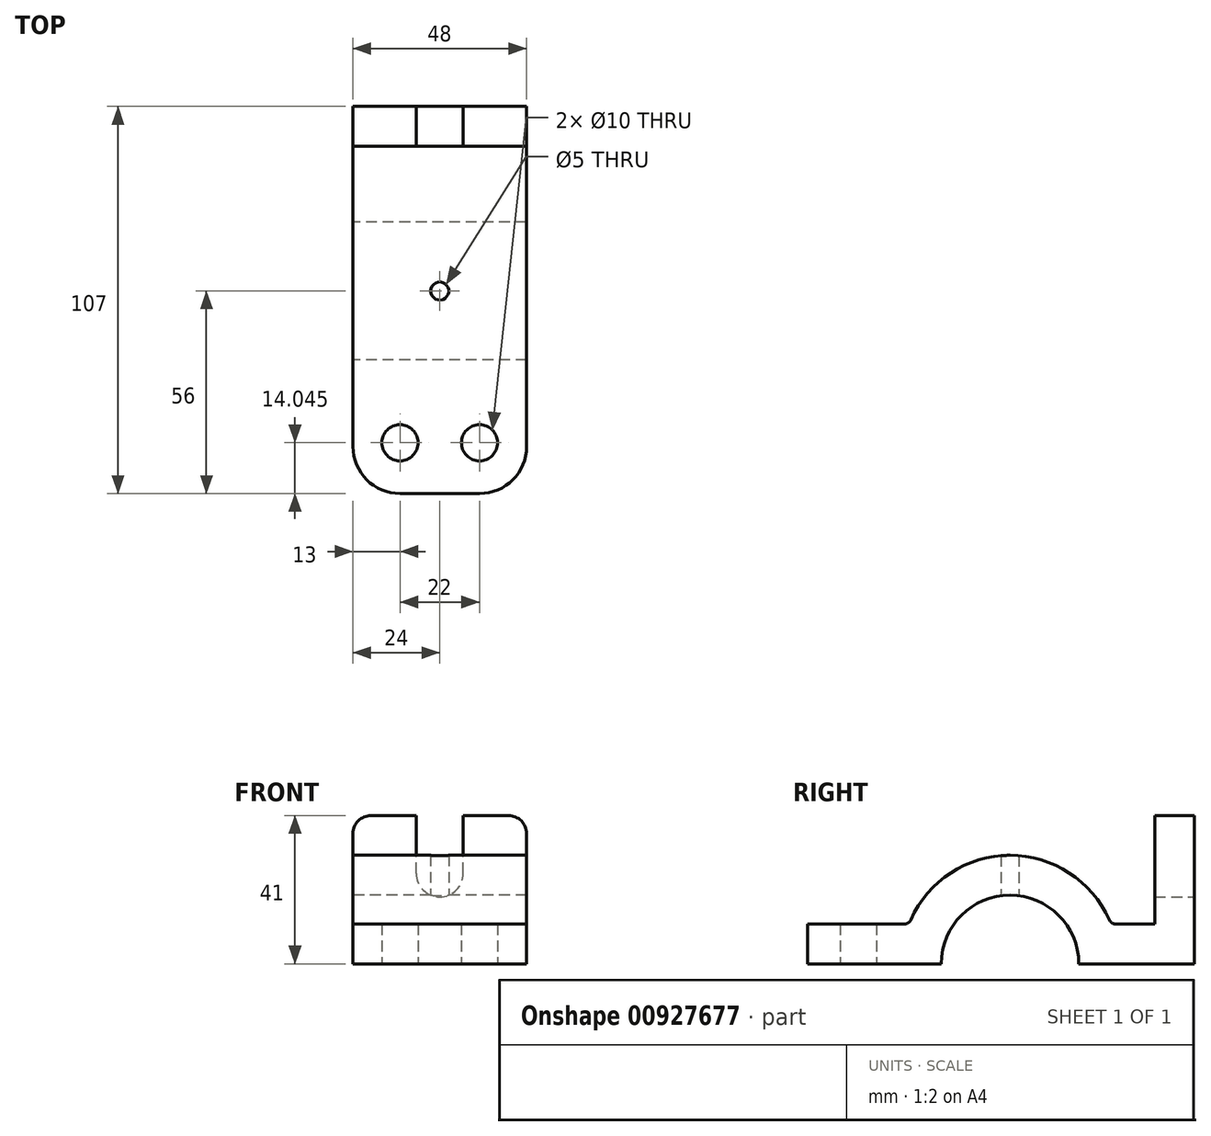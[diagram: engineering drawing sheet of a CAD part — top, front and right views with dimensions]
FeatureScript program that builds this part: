
annotation { "Feature Type Name" : "Feature", "Feature Type Description" : "" }
export const myFeature = defineFeature(function(context is Context, id is Id, definition is map)
    precondition{}
    {
        {
            var Q0;
            Q0=qCreatedBy(makeId("Right.planeOp"),FACE);
            var sketch = newSketch(context, id + "F0", { "sketchPlane" : qUnion([Q0])});
            skCircle(sketch, "E0", {"center": v(0, 0) * mm, "radius": 19 * mm});
            skCircle(sketch, "E1", {"center": v(0, 0) * mm, "radius": 30 * mm});
            skLineSegment(sketch, "E2.bottom", {"start": v(-56, 0) * mm, "end": v(51, 0) * mm});
            skLineSegment(sketch, "E2.top", {"start": v(-56, 11) * mm, "end": v(51, 11) * mm});
            skLineSegment(sketch, "E2.left", {"start": v(-56, 0) * mm, "end": v(-56, 11) * mm});
            skLineSegment(sketch, "E2.right", {"start": v(51, 0) * mm, "end": v(51, 11) * mm});
            skLineSegment(sketch, "E3.bottom", {"start": v(51, 11) * mm, "end": v(40, 11) * mm});
            skLineSegment(sketch, "E3.top", {"start": v(51, 41) * mm, "end": v(40, 41) * mm});
            skLineSegment(sketch, "E3.left", {"start": v(51, 11) * mm, "end": v(51, 41) * mm});
            skLineSegment(sketch, "E3.right", {"start": v(40, 11) * mm, "end": v(40, 41) * mm});
            skSolve(sketch);
        }
        {
            var Q0;
            {var subQ5=sQuery(id+"F0.wireOp",EDGE,"E2.left");Q0=makeQuery(id+"F0.imprint","IMPRINT",FACE,{"disambiguationData":[TD([[makeQuery(id+"F0.imprint","IMPRINT",EDGE,{"derivedFrom":subQ5}),-1.0]])]});}
            var Q1;
            {var subQ0=sQuery(id+"F0.wireOp",EDGE,"E2.bottom");var subQ1=sQuery(id+"F0.wireOp",EDGE,"E0");var subQ2=makeQuery(id+"F0.imprint","INTERSECT",VERTEX,{"disambiguationData":[OD(0.0)],"derivedFrom":[subQ1,subQ0]});Q1=makeQuery(id+"F0.imprint","IMPRINT",FACE,{"disambiguationData":[TD([[makeQuery(id+"F0.imprint","IMPRINT",EDGE,{"disambiguationData":[TD([[subQ2,1.0]])],"derivedFrom":subQ1}),-1.0]])]});}
            var Q2;
            {var subQ0=sQuery(id+"F0.wireOp",EDGE,"E2.top");var subQ1=sQuery(id+"F0.wireOp",EDGE,"E0");var subQ2=makeQuery(id+"F0.imprint","INTERSECT",VERTEX,{"disambiguationData":[OD(0.0)],"derivedFrom":[subQ1,subQ0]});Q2=makeQuery(id+"F0.imprint","IMPRINT",FACE,{"disambiguationData":[TD([[makeQuery(id+"F0.imprint","IMPRINT",EDGE,{"disambiguationData":[TD([[subQ2,1.0]])],"derivedFrom":subQ1}),-1.0]])]});}
            var Q3;
            {var subQ0=sQuery(id+"F0.wireOp",EDGE,"E2.top");var subQ1=sQuery(id+"F0.wireOp",EDGE,"E0");var subQ2=makeQuery(id+"F0.imprint","INTERSECT",VERTEX,{"disambiguationData":[OD(1.0)],"derivedFrom":[subQ1,subQ0]});Q3=makeQuery(id+"F0.imprint","IMPRINT",FACE,{"disambiguationData":[TD([[makeQuery(id+"F0.imprint","IMPRINT",EDGE,{"disambiguationData":[TD([[subQ2,1.0]])],"derivedFrom":subQ1}),-1.0]])]});}
            var Q4;
            {var subQ0=sQuery(id+"F0.wireOp",EDGE,"E2.right");Q4=makeQuery(id+"F0.imprint","IMPRINT",FACE,{"disambiguationData":[TD([[makeQuery(id+"F0.imprint","IMPRINT",EDGE,{"derivedFrom":subQ0}),1.0]])]});}
            var Q5;
            Q5=makeQuery(id+"F0.imprint","IMPRINT",FACE,{"disambiguationData":[TD([[makeQuery(id+"F0.imprint","IMPRINT",EDGE,{"derivedFrom":sQuery(id+"F0.wireOp",EDGE,"E3.top")}),1.0]])]});
            extrude(context, id + "F1", {"entities" : qUnion([Q0, Q1, Q2, Q3, Q4, Q5]), "endBound" : BoundingType.SYMMETRIC, "depth" : 48 * mm});
        }
        {
            var Q0;
            Q0=makeQuery(id+"F1.opExtrude","SWEPT_FACE",FACE,{"disambiguationData":[OSD([sQuery(id+"F0.wireOp",EDGE,"E2.right"),sQuery(id+"F0.wireOp",EDGE,"E3.left")])]});
            var sketch = newSketch(context, id + "F2", { "sketchPlane" : qUnion([Q0])});
            skLineSegment(sketch, "E4", {"start": v(0, 0) * mm, "end": v(0, 41) * mm, "construction": true});
            skCircle(sketch, "E5", {"center": v(0, 25) * mm, "radius": 6.5 * mm});
            skLineSegment(sketch, "E6", {"start": v(-6.5, 25) * mm, "end": v(-6.5, 41) * mm});
            skLineSegment(sketch, "E7", {"start": v(6.5, 25) * mm, "end": v(6.5, 41) * mm});
            skSolve(sketch);
        }
        {
            var Q0;
            {var subQ0=sQuery(id+"F2.wireOp",EDGE,"E5");var subQ2=makeQuery(id+"F2.imprint","INTERSECT",VERTEX,{"derivedFrom":[subQ0,sQuery(id+"F2.wireOp",EDGE,"E6")]});Q0=makeQuery(id+"F2.imprint","IMPRINT",FACE,{"disambiguationData":[TD([[makeQuery(id+"F2.imprint","IMPRINT",EDGE,{"disambiguationData":[TD([[subQ2,1.0]])],"derivedFrom":subQ0}),1.0]])]});}
            var Q1;
            {var subQ2=sQuery(id+"F2.wireOp",EDGE,"E6");Q1=makeQuery(id+"F2.imprint","IMPRINT",FACE,{"disambiguationData":[TD([[makeQuery(id+"F2.imprint","IMPRINT",EDGE,{"derivedFrom":subQ2}),-1.0]])]});}
            var Q2;
            Q2=makeQuery(id+"F1.opExtrude","SWEPT_FACE",FACE,{"disambiguationData":[OSD([sQuery(id+"F0.wireOp",EDGE,"E3.right")])]});
            extrude(context, id + "F3", {"entities" : qUnion([Q0, Q1]), "operationType" : NewBodyOperationType.REMOVE, "endBound" : BoundingType.UP_TO_SURFACE, "oppositeDirection" : true, "endBoundEntityFace" : qUnion([Q2]), "depth" : 25 * mm});
        }
        {
            var Q0;
            {var subQ0=sQuery(id+"F0.wireOp",EDGE,"E2.bottom");Q0=makeQuery(id+"F1.opExtrude","SWEPT_FACE",FACE,{"disambiguationData":[OSD([subQ0]),TDD([makeQuery(id+"F0.imprint","IMPRINT",EDGE,{"disambiguationData":[TD([[makeQuery(id+"F0.imprint","INTERSECT",VERTEX,{"derivedFrom":[subQ0,sQuery(id+"F0.wireOp",EDGE,"E2.left")]}),-1.0]])],"derivedFrom":subQ0}),makeQuery(id+"F0.imprint","IMPRINT",EDGE,{"disambiguationData":[TD([[makeQuery(id+"F0.imprint","INTERSECT",VERTEX,{"disambiguationData":[OD(0.0)],"derivedFrom":[sQuery(id+"F0.wireOp",EDGE,"E0"),subQ0]}),1.0]])],"derivedFrom":subQ0})])]});}
            var sketch = newSketch(context, id + "F4", { "sketchPlane" : qUnion([Q0])});
            skCircle(sketch, "E8", {"center": v(0, 0) * mm, "radius": 2.5 * mm});
            skLineSegment(sketch, "E9", {"start": v(24, 41.96) * mm, "end": v(-24, 41.96) * mm, "construction": true});
            skLineSegment(sketch, "E10", {"start": v(0, 27.91) * mm, "end": v(0, 56) * mm, "construction": true});
            skCircle(sketch, "E11", {"center": v(-11, 41.96) * mm, "radius": 5 * mm});
            skCircle(sketch, "E12", {"center": v(11, 41.96) * mm, "radius": 5 * mm});
            skSolve(sketch);
        }
        {
            var Q0;
            Q0=qSketchRegion(id+"F4",true);
            extrude(context, id + "F5", {"entities" : qUnion([Q0]), "operationType" : NewBodyOperationType.REMOVE, "endBound" : BoundingType.THROUGH_ALL, "oppositeDirection" : true, "depth" : 25 * mm, "offsetDistance" : 25 * mm});
        }
        {
            var Q0;
            Q0=makeQuery(id+"F1.opExtrude","CAP_EDGE",EDGE,{"disambiguationData":[OSD([sQuery(id+"F0.wireOp",EDGE,"E2.left")])],"isStart":false});
            var Q1;
            Q1=makeQuery(id+"F1.opExtrude","CAP_EDGE",EDGE,{"disambiguationData":[OSD([sQuery(id+"F0.wireOp",EDGE,"E2.left")])],"isStart":true});
            fillet(context, id + "F6", {"entities" : qUnion([Q0, Q1]), "radius" : 13 * mm, "tangentPropagation" : true, "allowEdgeOverflow" : false});
        }
        {
            var Q0;
            Q0=makeQuery(id+"F1.opExtrude","CAP_EDGE",EDGE,{"disambiguationData":[OSD([sQuery(id+"F0.wireOp",EDGE,"E3.top")])],"isStart":false});
            var Q1;
            Q1=makeQuery(id+"F1.opExtrude","CAP_EDGE",EDGE,{"disambiguationData":[OSD([sQuery(id+"F0.wireOp",EDGE,"E3.top")])],"isStart":true});
            fillet(context, id + "F7", {"entities" : qUnion([Q0, Q1]), "radius" : 5 * mm, "tangentPropagation" : true, "allowEdgeOverflow" : false});
        }
        {
            var Q0;
            {var subQ0=sQuery(id+"F0.wireOp",EDGE,"E2.top");var subQ1=sQuery(id+"F0.wireOp",EDGE,"E1");Q0=makeQuery(id+"F1.opExtrude","SWEPT_EDGE",EDGE,{"disambiguationData":[OSD([subQ1,subQ0]),TDD([makeQuery(id+"F0.imprint","INTERSECT",VERTEX,{"disambiguationData":[OD(1.0)],"derivedFrom":[subQ1,subQ0]})])]});}
            var Q1;
            {var subQ0=sQuery(id+"F0.wireOp",EDGE,"E2.top");var subQ1=sQuery(id+"F0.wireOp",EDGE,"E1");Q1=makeQuery(id+"F1.opExtrude","SWEPT_EDGE",EDGE,{"disambiguationData":[OSD([subQ1,subQ0]),TDD([makeQuery(id+"F0.imprint","INTERSECT",VERTEX,{"disambiguationData":[OD(0.0)],"derivedFrom":[subQ1,subQ0]})])]});}
            fillet(context, id + "F8", {"entities" : qUnion([Q0, Q1]), "radius" : 2 * mm, "tangentPropagation" : true, "allowEdgeOverflow" : false});
        }
    });
